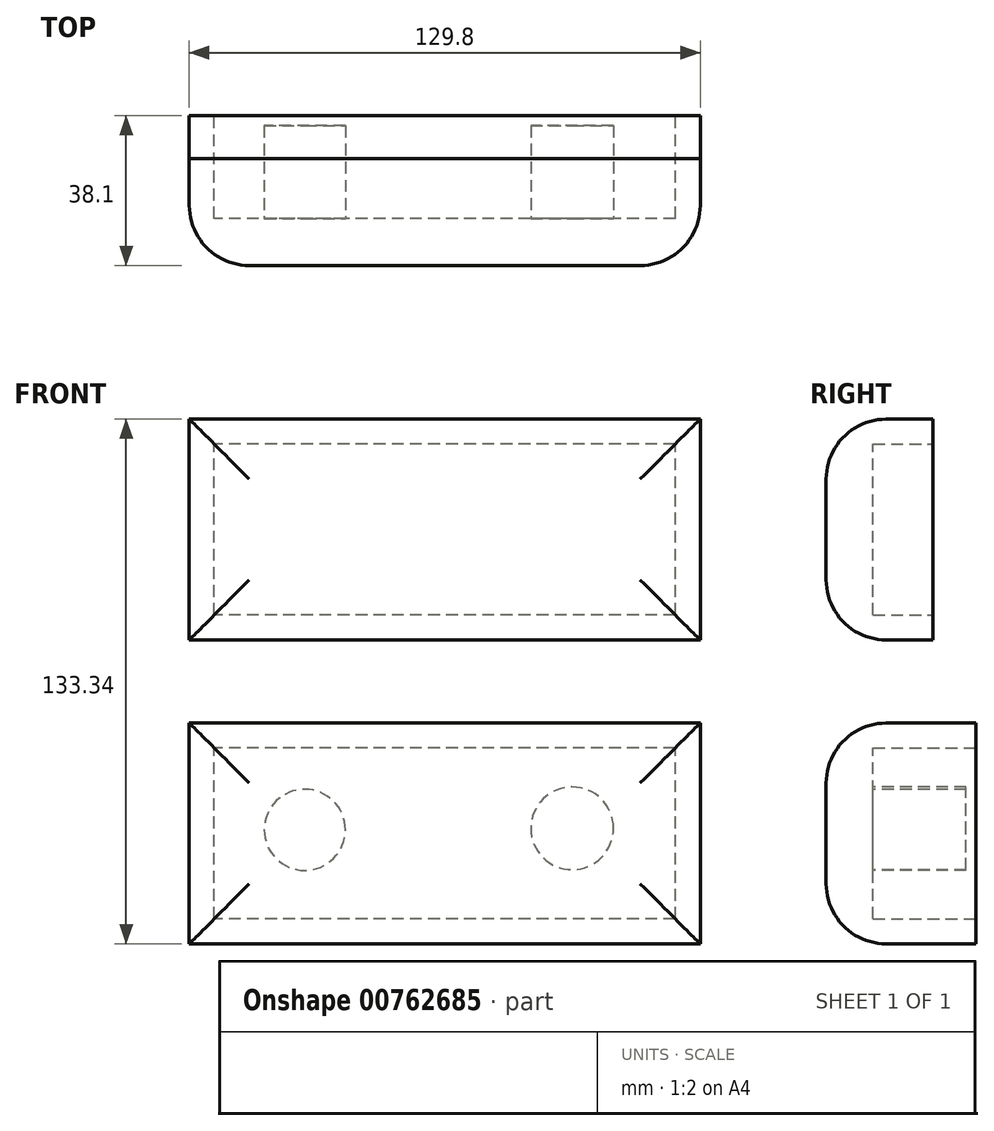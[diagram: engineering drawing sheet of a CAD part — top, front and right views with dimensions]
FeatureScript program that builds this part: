
annotation { "Feature Type Name" : "Feature", "Feature Type Description" : "" }
export const myFeature = defineFeature(function(context is Context, id is Id, definition is map)
    precondition{}
    {
        {
            var Q0;
            Q0=qCreatedBy(makeId("Front.planeOp"),FACE);
            var sketch = newSketch(context, id + "F0", { "sketchPlane" : qUnion([Q0])});
            skLineSegment(sketch, "E0.bottom", {"start": v(64.9, -28.06) * mm, "end": v(-64.9, -28.06) * mm});
            skLineSegment(sketch, "E0.top", {"start": v(64.9, 28.06) * mm, "end": v(-64.9, 28.06) * mm});
            skLineSegment(sketch, "E0.left", {"start": v(64.9, -28.06) * mm, "end": v(64.9, 28.06) * mm});
            skLineSegment(sketch, "E0.right", {"start": v(-64.9, -28.06) * mm, "end": v(-64.9, 28.06) * mm});
            skPoint(sketch, "E0.middle", {"position": v(0, 0) * mm});
            skSolve(sketch);
        }
        {
            var Q0;
            Q0 = qSketchRegion(id + "F0", true);
            extrude(context, id + "F1", {"entities" : qUnion([Q0]), "depth" : 38.1 * mm, "offsetDistance" : 25.4 * mm});
        }
        {
            var Q0;
            Q0=makeQuery(id+"F1.opExtrude","CAP_EDGE",EDGE,{"disambiguationData":[OSD([sQuery(id+"F0.wireOp",EDGE,"E0.bottom")])],"isStart":false});
            var Q1;
            Q1=makeQuery(id+"F1.opExtrude","CAP_EDGE",EDGE,{"disambiguationData":[OSD([sQuery(id+"F0.wireOp",EDGE,"E0.top")])],"isStart":false});
            var Q2;
            Q2=makeQuery(id+"F1.opExtrude","CAP_EDGE",EDGE,{"disambiguationData":[OSD([sQuery(id+"F0.wireOp",EDGE,"E0.right")])],"isStart":false});
            var Q3;
            Q3=makeQuery(id+"F1.opExtrude","CAP_EDGE",EDGE,{"disambiguationData":[OSD([sQuery(id+"F0.wireOp",EDGE,"E0.left")])],"isStart":false});
            fillet(context, id + "F2", {"entities" : qUnion([Q0, Q1, Q2, Q3]), "radius" : 15.24 * mm, "tangentPropagation" : true, "allowEdgeOverflow" : false});
        }
        {
            var Q0;
            Q0=qCreatedBy(makeId("Front.planeOp"),FACE);
            cPlane(context, id + "F3", {"entities" : qUnion([Q0]), "cplaneType" : CPlaneType.OFFSET, "offset" : 17.53 * mm, "width" : 152.4 * mm, "height" : 152.4 * mm});
        }
        {
            var Q0;
            Q0=makeQuery(id+"F0.imprint","IMPRINT",FACE,{"disambiguationData":[TD([[makeQuery(id+"F0.imprint","IMPRINT",EDGE,{"derivedFrom":sQuery(id+"F0.wireOp",EDGE,"E0.bottom")}),-1.0]])]});
            var sketch = newSketch(context, id + "F4", { "sketchPlane" : qUnion([Q0])});
            skLineSegment(sketch, "E1.0", {"start": v(-64.9, -28.06) * mm, "end": v(-64.9, 28.06) * mm});
            skLineSegment(sketch, "E1.1", {"start": v(64.9, -28.06) * mm, "end": v(64.9, 28.06) * mm});
            skLineSegment(sketch, "E1.2", {"start": v(64.9, 28.06) * mm, "end": v(-64.9, 28.06) * mm});
            skLineSegment(sketch, "E1.3", {"start": v(64.9, -28.06) * mm, "end": v(-64.9, -28.06) * mm});
            skLineSegment(sketch, "E2.0", {"start": v(-58.55, -21.71) * mm, "end": v(-58.55, 21.71) * mm});
            skLineSegment(sketch, "E2.1", {"start": v(58.55, -21.71) * mm, "end": v(-58.55, -21.71) * mm});
            skLineSegment(sketch, "E2.2", {"start": v(58.55, -21.71) * mm, "end": v(58.55, 21.71) * mm});
            skLineSegment(sketch, "E2.3", {"start": v(58.55, 21.71) * mm, "end": v(-58.55, 21.71) * mm});
            skSolve(sketch);
        }
        {
            var Q0;
            Q0=makeQuery(id+"F4.imprint","IMPRINT",FACE,{"disambiguationData":[TD([[makeQuery(id+"F4.imprint","IMPRINT",EDGE,{"derivedFrom":sQuery(id+"F4.wireOp",EDGE,"E2.0")}),-1.0]])]});
            extrude(context, id + "F5", {"entities" : qUnion([Q0]), "operationType" : NewBodyOperationType.REMOVE, "depth" : 26.16 * mm, "offsetDistance" : 25.4 * mm});
        }
        {
            var Q0;
            Q0=makeQuery(id+"F1.opExtrude","SWEPT_BODY",BODY,{"disambiguationData":[OSD([sQuery(id+"F0.wireOp",EDGE,"E0.bottom"),sQuery(id+"F0.wireOp",EDGE,"E0.top"),sQuery(id+"F0.wireOp",EDGE,"E0.left"),sQuery(id+"F0.wireOp",EDGE,"E0.right")])]});
            transform(context, id + "F6", {"entities" : qUnion([Q0]), "transformType" : TransformType.TRANSLATION_3D, "dx" : 0 * mm, "dy" : 0 * mm, "dz" : 77.22 * mm, "makeCopy" : true});
        }
        {
            var Q0;
            Q0=qCreatedBy(id+"F3.planeOp",FACE);
            cPlane(context, id + "F7", {"entities" : qUnion([Q0]), "cplaneType" : CPlaneType.OFFSET, "offset" : 9.9 * mm, "width" : 152.4 * mm, "height" : 152.4 * mm});
        }
        {
            var Q0;
            Q0=qCreatedBy(id+"F7.planeOp",FACE);
            var sketch = newSketch(context, id + "F8", { "sketchPlane" : qUnion([Q0])});
            skCircle(sketch, "E3", {"center": v(-35.55, 0.92) * mm, "radius": 10.3 * mm});
            skPoint(sketch, "E3.first.point", {"position": v(-45.73, 2.5) * mm});
            skPoint(sketch, "E3.second.point", {"position": v(-25.28, 1.66) * mm});
            skPoint(sketch, "E3.third.point", {"position": v(-25.86, 4.42) * mm});
            skSolve(sketch);
        }
        {
            var Q0;
            Q0 = qSketchRegion(id + "F8", true);
            extrude(context, id + "F9", {"entities" : qUnion([Q0]), "operationType" : NewBodyOperationType.ADD, "oppositeDirection" : true, "depth" : 24.9 * mm, "offsetDistance" : 25.4 * mm});
        }
        {
            var Q0;
            Q0=qCreatedBy(id+"F7.planeOp",FACE);
            var sketch = newSketch(context, id + "F10", { "sketchPlane" : qUnion([Q0])});
            skCircle(sketch, "E4", {"center": v(32.37, 1.3) * mm, "radius": 10.5 * mm});
            skPoint(sketch, "E4.first.point", {"position": v(24.68, 8.44) * mm});
            skPoint(sketch, "E4.second.point", {"position": v(40.14, -5.75) * mm});
            skPoint(sketch, "E4.third.point", {"position": v(42.78, 0) * mm});
            skSolve(sketch);
        }
        {
            var Q0;
            Q0 = qSketchRegion(id + "F10", true);
            extrude(context, id + "F11", {"entities" : qUnion([Q0]), "operationType" : NewBodyOperationType.ADD, "oppositeDirection" : true, "depth" : 24.9 * mm, "offsetDistance" : 25.4 * mm});
        }
        {
            var Q0;
            Q0=makeQuery(id+"F6.opPattern","COPY",FACE,{"derivedFrom":makeQuery(id+"F1.opExtrude","CAP_FACE",FACE,{"disambiguationData":[OSD([sQuery(id+"F0.wireOp",EDGE,"E0.bottom"),sQuery(id+"F0.wireOp",EDGE,"E0.top"),sQuery(id+"F0.wireOp",EDGE,"E0.left"),sQuery(id+"F0.wireOp",EDGE,"E0.right")])],"isStart":true}),"instanceName":"1"});
            extrude(context, id + "F12", {"entities" : qUnion([Q0]), "operationType" : NewBodyOperationType.REMOVE, "oppositeDirection" : true, "depth" : 10.92 * mm, "offsetDistance" : 25.4 * mm});
        }
    });
